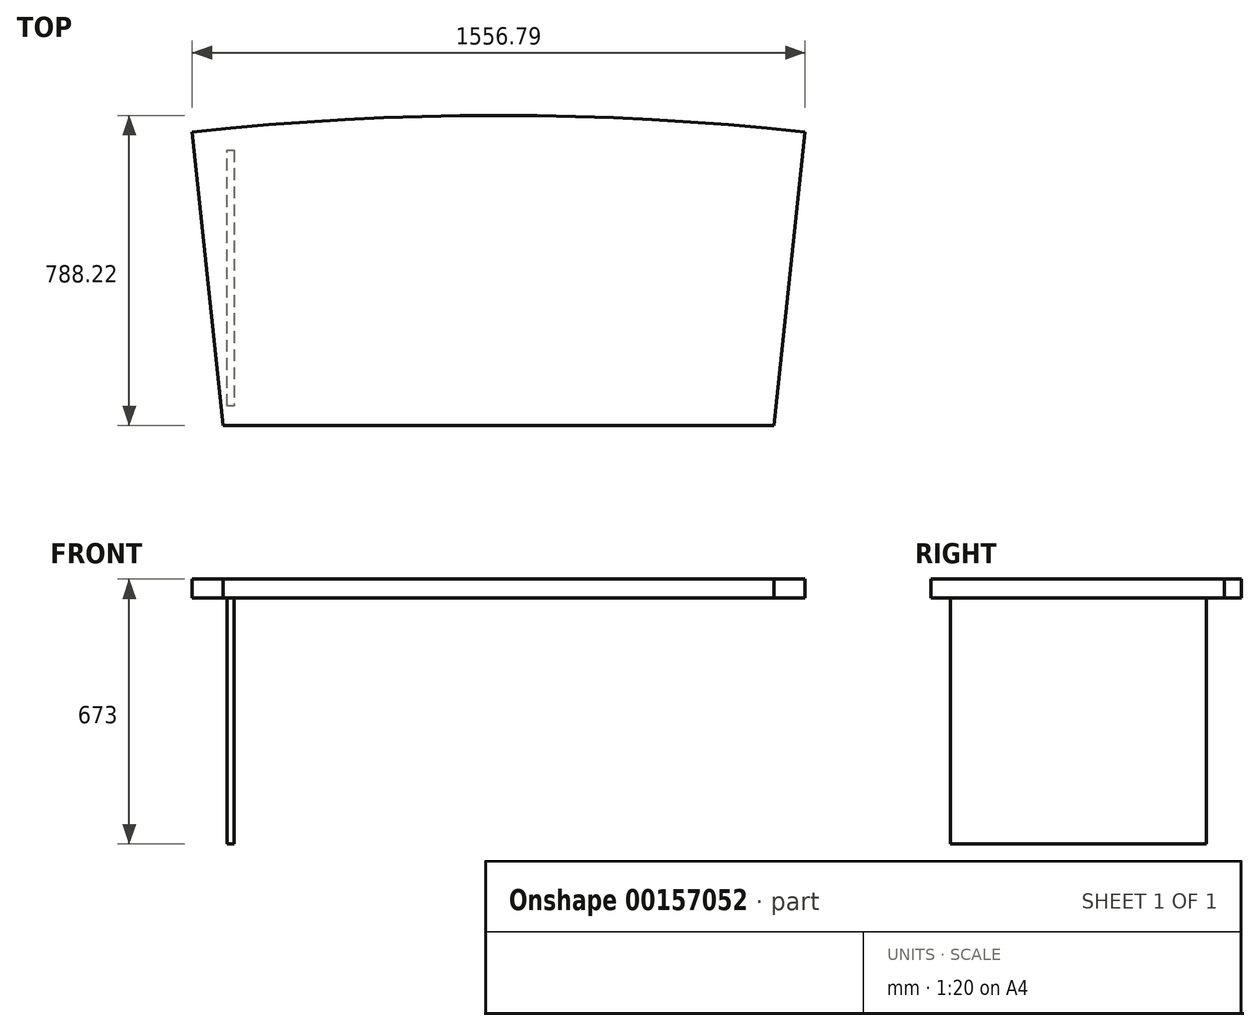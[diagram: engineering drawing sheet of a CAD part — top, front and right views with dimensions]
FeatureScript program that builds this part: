
annotation { "Feature Type Name" : "Feature", "Feature Type Description" : "" }
export const myFeature = defineFeature(function(context is Context, id is Id, definition is map)
    precondition{}
    {
        {
            var Q0;
            Q0=qCreatedBy(makeId("Top.planeOp"),FACE);
            var sketch = newSketch(context, id + "F0", { "sketchPlane" : qUnion([Q0])});
            skLineSegment(sketch, "E0", {"start": v(-668.34, -382.44) * mm, "end": v(731.66, -382.44) * mm});
            skLineSegment(sketch, "E1", {"start": v(731.66, -382.44) * mm, "end": v(810.05, 363.46) * mm});
            skLineSegment(sketch, "E2", {"start": v(-668.34, -382.44) * mm, "end": v(-746.74, 363.46) * mm});
            skArc(sketch, "E3", {"start": v(810.05, 363.46) * mm, "mid": v(31.66, 405.78) * mm, "end": v(-746.74, 363.46) * mm});
            skSolve(sketch);
        }
        {
            var Q0;
            Q0 = qSketchRegion(id + "F0", true);
            var Q1;
            Q1=makeQuery(id+"F0.imprint","IMPRINT",FACE,{"disambiguationData":[TD([[makeQuery(id+"F0.imprint","IMPRINT",EDGE,{"derivedFrom":sQuery(id+"F0.wireOp",EDGE,"E0")}),1.0]])]});
            extrude(context, id + "F1", {"entities" : qUnion([Q0, Q1]), "depth" : 48 * mm});
        }
        {
            var Q0;
            Q0=makeQuery(id+"F0.imprint","IMPRINT",FACE,{"disambiguationData":[TD([[makeQuery(id+"F0.imprint","IMPRINT",EDGE,{"derivedFrom":sQuery(id+"F0.wireOp",EDGE,"E0")}),1.0]])]});
            var sketch = newSketch(context, id + "F2", { "sketchPlane" : qUnion([Q0])});
            skLineSegment(sketch, "E4", {"start": v(-658.34, -332.44) * mm, "end": v(-658.34, 317.56) * mm});
            skLineSegment(sketch, "E5", {"start": v(-658.34, 317.56) * mm, "end": v(-640.34, 317.56) * mm});
            skLineSegment(sketch, "E6", {"start": v(-640.34, 317.56) * mm, "end": v(-640.34, -332.44) * mm});
            skLineSegment(sketch, "E7", {"start": v(-640.34, -332.44) * mm, "end": v(-658.34, -332.44) * mm});
            skSolve(sketch);
        }
        {
            var Q0;
            Q0 = qSketchRegion(id + "F2", true);
            extrude(context, id + "F3", {"entities" : qUnion([Q0]), "oppositeDirection" : true, "depth" : 625 * mm});
        }
    });
